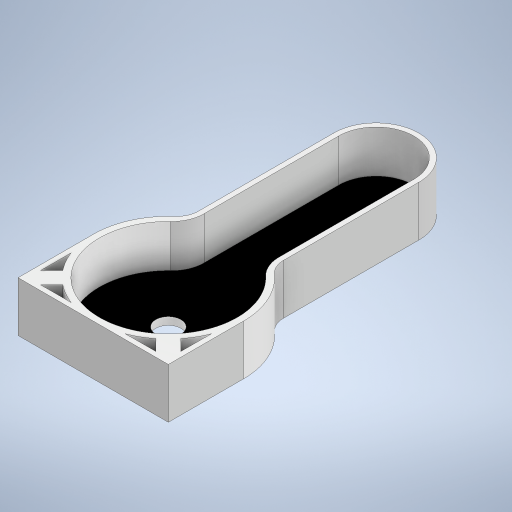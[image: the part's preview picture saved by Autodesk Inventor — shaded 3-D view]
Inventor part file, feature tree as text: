
AUTODESK INVENTOR PART (.ipt)
format: ipt  version: 2024 (Build 280153020, 153B)  size: 382,976 bytes
history: native  units: mm
features: sketch x14, extrude x13, fillet x4
ambient origin geometry x8: Origin, YZ Plane, XZ Plane, XY Plane, X Axis, Y Axis, Z Axis, Center Point
bodies: Solid1 (feature_tree)
feature tree (31):
  extrude  "Extrusion1"  Depth=20.0mm TaperAngle=0.0deg
  extrude  "Extrusion2"  Depth=17.0mm TaperAngle=0.0deg
  extrude  "Extrusion3"  Depth=5.0mm TaperAngle=0.0deg
  extrude  "Extrusion6"  Depth=60.0mm
  extrude  "Extrusion7"  Depth=20.0mm TaperAngle=0.0deg
  fillet  "Fillet1"  Radius=13.0mm
  fillet  "Fillet2"  Radius=9.0mm
  fillet  "Fillet3"  Radius=13.0mm
  fillet  "Fillet4"  Radius=9.0mm
  extrude  "Extrusion8"  Depth=20.0mm TaperAngle=0.0deg
  extrude  "Extrusion9"  Depth=20.0mm TaperAngle=0.0deg
  extrude  "Extrusion10"  Depth=3.0mm TaperAngle=0.0deg
  sketch  "Sketch17"  dims[d53=135.0deg d54=5.0mm]
  extrude  "Extrusion15"  Depth=5.0mm
  extrude  "Extrusion16"  Depth=5.0mm
  extrude  "Extrusion17"  Depth=20.0mm TaperAngle=0.0deg
  extrude  "Extrusion19"  Depth=5.0mm
  extrude  "Extrusion20"  TaperAngle=135.0deg  [1 undecoded]
  sketch  "Sketch2"  dims[d0=60.0mm d1=20.0mm d2=0.0mm]
  sketch  "Sketch3"  dims[d3=55.0mm d4=17.0mm d5=0.0mm]
  sketch  "Sketch4"  dims[d6=10.0mm d7=5.0mm d8=0.0mm]
  sketch  "Sketch9"  dims[d15=17.0mm d16=0.0mm d17=60.0mm]
  sketch  "Sketch10"  dims[d18=60.0mm d19=20.0mm d20=0.0mm d21=13.0mm d22=9.0mm d23=13.0mm d24=9.0mm]
  sketch  "Sketch12"  dims[d25=3.0mm d26=0.0mm d27=20.0mm d28=0.0mm]
  sketch  "Sketch13"  dims[d29=20.0mm d30=0.0mm d45=20.0mm d46=0.0mm]
  sketch  "Sketch14"  dims[d47=3.0mm d48=0.0mm d49=3.0mm d50=0.0mm]
  sketch  "Sketch21"  dims[d55=135.0deg d56=5.0mm]
  sketch  "Sketch22"  dims[d57=135.0deg d58=20.0mm d59=0.0mm]
  sketch  "Sketch23"  dims[d60=45.0deg d61=5.0mm]
  sketch  "Sketch25"  dims[d62=5.0mm d63=135.0deg]
  sketch  "Sketch27"  dims[d64=45.0deg d65=20.0mm d66=0.0mm d10=0.5mm d11=0.872665mm d12=0.5mm d13=0.872665mm]
note: 1 required parameter value undecoded (feature->parameter linkage not recoverable at this tier; creation-order binding heuristic only, values carry confidence <= 0.55)
